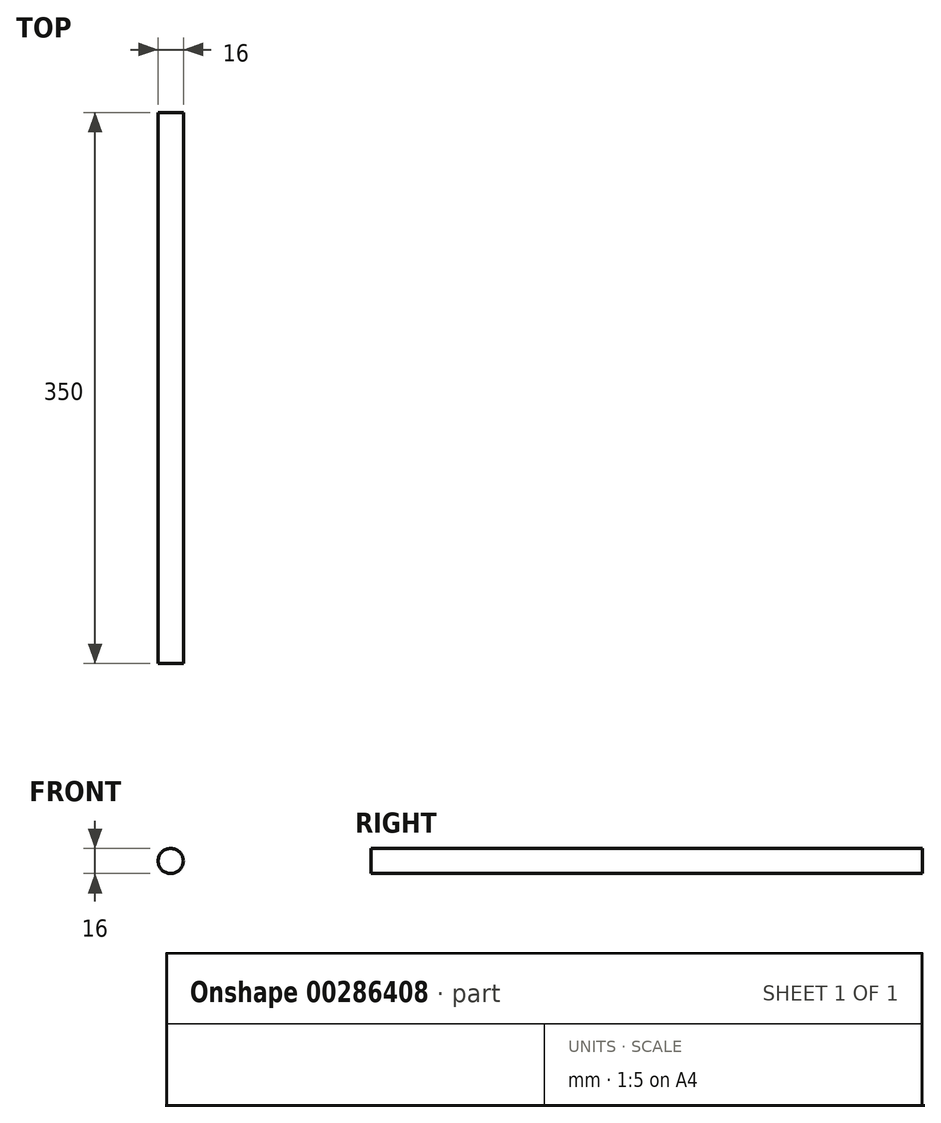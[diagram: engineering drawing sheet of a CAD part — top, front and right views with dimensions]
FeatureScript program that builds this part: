
annotation { "Feature Type Name" : "Feature", "Feature Type Description" : "" }
export const myFeature = defineFeature(function(context is Context, id is Id, definition is map)
    precondition{}
    {
        {
            var Q0;
            Q0=qCreatedBy(makeId("Front.planeOp"),FACE);
            var sketch = newSketch(context, id + "F0", { "sketchPlane" : qUnion([Q0])});
            skCircle(sketch, "E0", {"center": v(0, 0) * mm, "radius": 8 * mm});
            skSolve(sketch);
        }
        {
            var Q0;
            Q0 = qSketchRegion(id + "F0", true);
            extrude(context, id + "F1", {"entities" : qUnion([Q0]), "depth" : 350 * mm});
        }
    });
